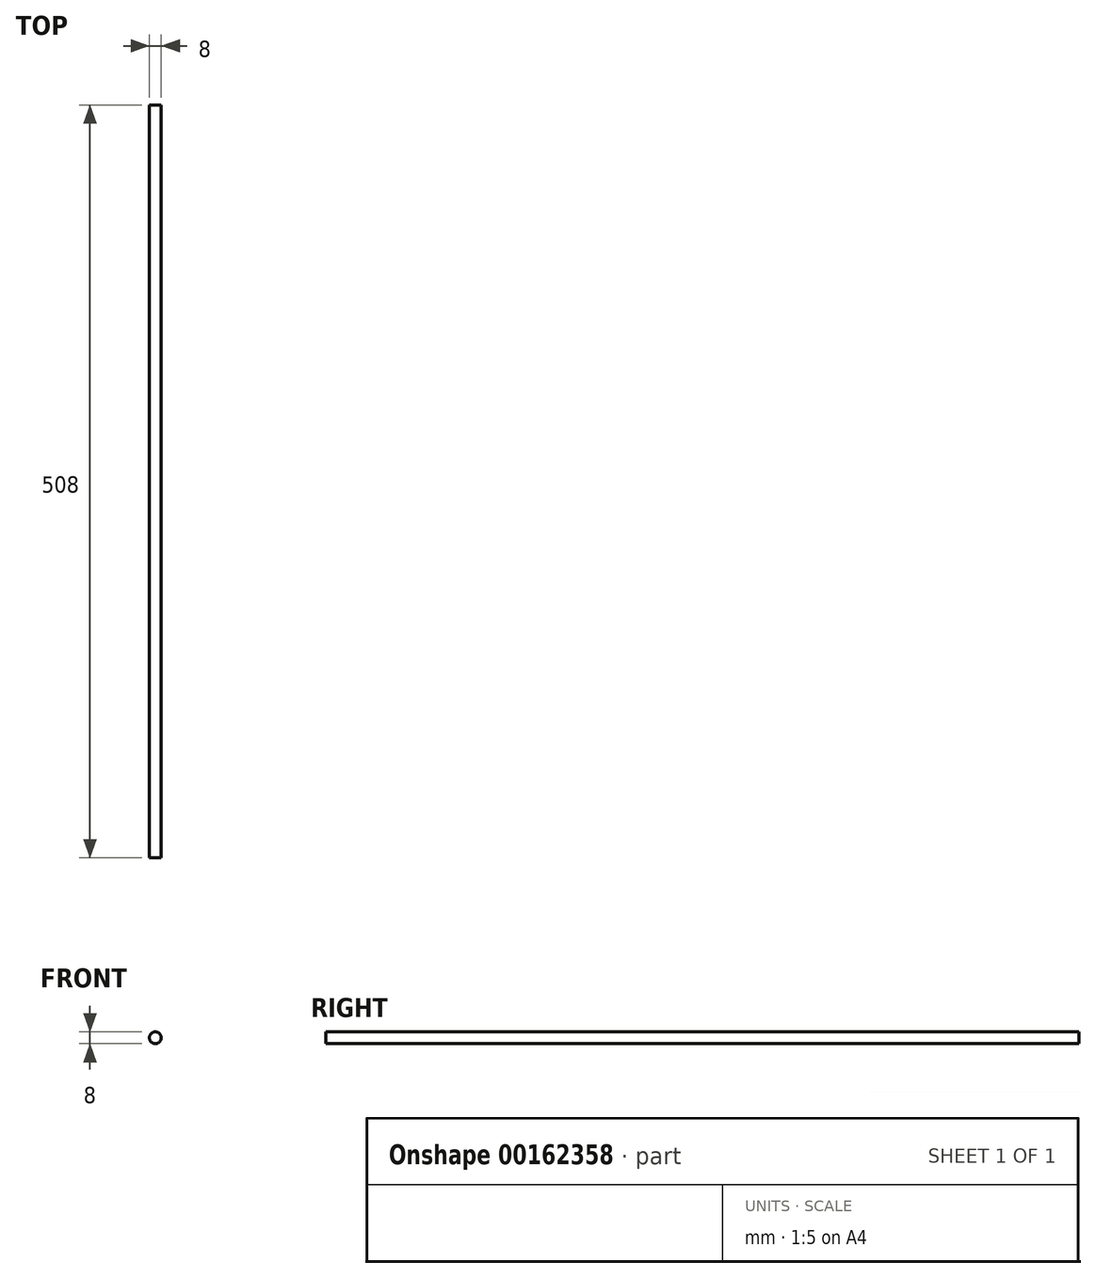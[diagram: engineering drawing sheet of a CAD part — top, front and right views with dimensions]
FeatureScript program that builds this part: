
annotation { "Feature Type Name" : "Feature", "Feature Type Description" : "" }
export const myFeature = defineFeature(function(context is Context, id is Id, definition is map)
    precondition{}
    {
        {
            var Q0;
            Q0=qCreatedBy(makeId("Front.planeOp"),FACE);
            var sketch = newSketch(context, id + "F0", { "sketchPlane" : qUnion([Q0])});
            skCircle(sketch, "E0", {"center": v(0, 0) * mm, "radius": 4 * mm});
            skSolve(sketch);
        }
        {
            var Q0;
            Q0=makeQuery(id+"F0.imprint","IMPRINT",FACE,{"disambiguationData":[TD([[makeQuery(id+"F0.imprint","IMPRINT",EDGE,{"derivedFrom":sQuery(id+"F0.wireOp",EDGE,"E0")}),1.0]])]});
            extrude(context, id + "F1", {"entities" : qUnion([Q0]), "depth" : 508 * mm});
        }
    });
